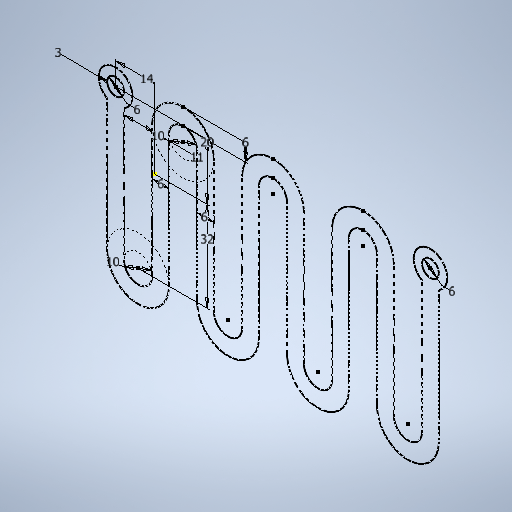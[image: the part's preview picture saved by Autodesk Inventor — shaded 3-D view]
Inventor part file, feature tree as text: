
AUTODESK INVENTOR PART (.ipt)
format: ipt  version: 2025.2 (Build 292293000, 293)  size: 291,328 bytes
history: native  units: mm
features: sketch x1
ambient origin geometry x8: Origin, YZ Plane, XZ Plane, XY Plane, X Axis, Y Axis, Z Axis, Center Point
feature tree (1):
  sketch  "Sketch1"  dims[d1=20.0mm d2=14.0mm d7=11.0mm d8=6.0mm d9=3.0mm d16=10.0mm d20=32.0mm d25=6.0mm d29=10.0mm d36=6.0mm d39=6.0mm d41=6.0mm]
